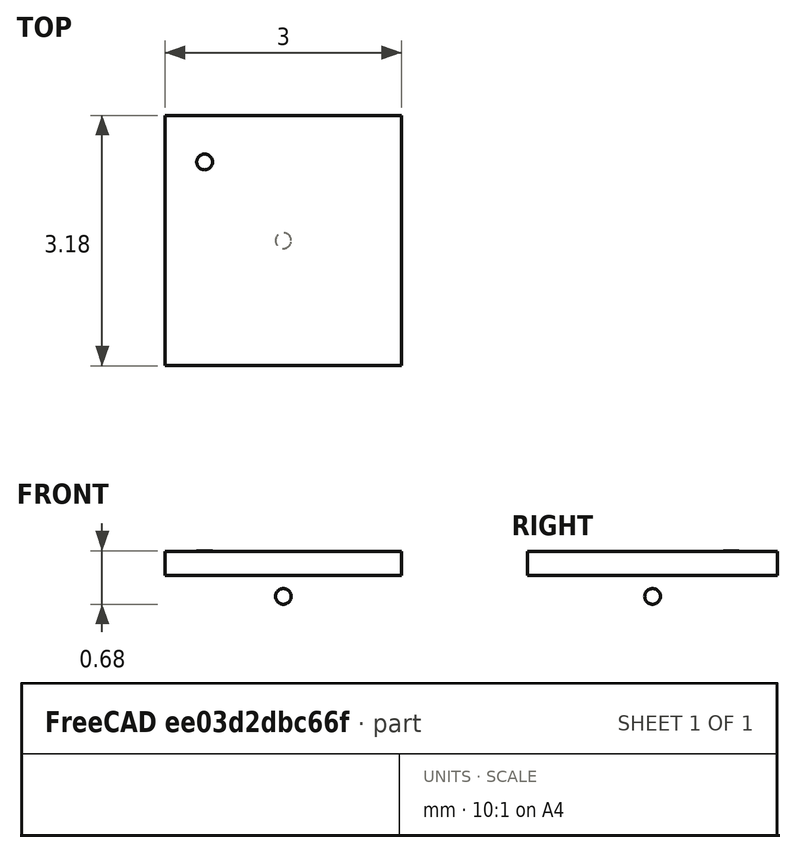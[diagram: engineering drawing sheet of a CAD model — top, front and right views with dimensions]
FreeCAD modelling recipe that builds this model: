
FCSTD DOCUMENT  (FreeCAD 1.0R39109 (Git))
Label: Nordic_WLCSP_3.175x3.175mm_P0.35mm
License: All rights reserved
LicenseURL: https://en.wikipedia.org/wiki/All_rights_reserved
objects: App::LinkElement×81, Sketcher::SketchObject×1, PartDesign::Pad×1, PartDesign::Body×1, Part::Sphere×1, Part::Cylinder×1, Part::FeaturePython×1, App::Part×1
note: 8 computed .brp shape members not serialized (recipe doc carries the construction recipe); baked Part::Feature solids carry a one-line shape summary decoded from their .brp

FEATURE [Sketcher::SketchObject] Sketch
  ArcFitTolerance = 1e-06
  AttachmentSupport = -> [XY_Plane001]
  FullyConstrained = true
  MakeInternals = false
  MapMode = 5
  sketch-geometry (5):
    g0: LineSegment StartX=-1.5 StartY=-1.5875 StartZ=0 EndX=1.5 EndY=-1.5875 EndZ=0
    g1: LineSegment StartX=1.5 StartY=-1.5875 StartZ=0 EndX=1.5 EndY=1.5875 EndZ=0
    g2: LineSegment StartX=1.5 StartY=1.5875 StartZ=0 EndX=-1.5 EndY=1.5875 EndZ=0
    g3: LineSegment StartX=-1.5 StartY=1.5875 StartZ=0 EndX=-1.5 EndY=-1.5875 EndZ=0
    g4: GeomPoint [constr] X=0 Y=0 Z=0
  constraints (12):
    c: Coincident(g0,g1)
    c: Coincident(g1,g2)
    c: Coincident(g2,g3)
    c: Coincident(g3,g0)
    c: Horizontal(g0)
    c: Horizontal(g2)
    c: Vertical(g1)
    c: Vertical(g3)
    c: Symmetric(g2,g0,g4)
    c: Distance(g1,g3) = 3
    c: Distance(g0,g2) = 3.175
    c: Coincident(g4,g-1)
FEATURE [PartDesign::Pad] Pad
  Direction = (0,0,1)
  Length = 0.3
  Length2 = 10
  Profile = -> Sketch
  ReferenceAxis = -> Sketch [N_Axis]
  Refine = true
  Suppressed = false
  Type = 0
FEATURE [PartDesign::Body] Body
  AllowCompound = false
  Group = -> [Sketch,Pad]
  Origin = -> Origin001
  Placement = pos=(0,0,0.18) rot=(0,0,1;0rad)
  Tip = -> Pad
FEATURE [Part::Sphere] Sphere
  Angle1 = -90
  Angle2 = 90
  Angle3 = 360
  AttacherType = Attacher::AttachEngine3D
  Placement = pos=(0,0,-0.089) rot=(0,0,1;0rad)
  Radius = 0.1
FEATURE [Part::Cylinder] Cylinder
  Angle = 360
  AttacherType = Attacher::AttachEngine3D
  FirstAngle = 0
  Height = 0.02
  Placement = pos=(-1,1,0.47) rot=(0,0,1;0rad)
  Radius = 0.1
  SecondAngle = 0
FEATURE [App::LinkElement] Array_i0
  LinkPlacement = pos=(0,0,-0.089) rot=(0,0,1;0rad)
  LinkedObject = -> Sphere
  Placement = pos=(0,0,-0.089) rot=(0,0,1;0rad)
  _LinkOwner = 918
FEATURE [App::LinkElement] Array_i1
  LinkPlacement = pos=(0,0.35,-0.089) rot=(0,0,1;0rad)
  LinkedObject = -> Sphere
  Placement = pos=(0,0.35,-0.089) rot=(0,0,1;0rad)
  _LinkOwner = 918
FEATURE [App::LinkElement] Array_i2
  LinkPlacement = pos=(0,0.7,-0.089) rot=(0,0,1;0rad)
  LinkedObject = -> Sphere
  Placement = pos=(0,0.7,-0.089) rot=(0,0,1;0rad)
  _LinkOwner = 918
FEATURE [App::LinkElement] Array_i3
  LinkPlacement = pos=(0,1.05,-0.089) rot=(0,0,1;0rad)
  LinkedObject = -> Sphere
  Placement = pos=(0,1.05,-0.089) rot=(0,0,1;0rad)
  _LinkOwner = 918
FEATURE [App::LinkElement] Array_i4
  LinkPlacement = pos=(0,1.4,-0.089) rot=(0,0,1;0rad)
  LinkedObject = -> Sphere
  Placement = pos=(0,1.4,-0.089) rot=(0,0,1;0rad)
  _LinkOwner = 918
FEATURE [App::LinkElement] Array_i5
  LinkPlacement = pos=(0,1.75,-0.089) rot=(0,0,1;0rad)
  LinkedObject = -> Sphere
  Placement = pos=(0,1.75,-0.089) rot=(0,0,1;0rad)
  _LinkOwner = 918
FEATURE [App::LinkElement] Array_i6
  LinkPlacement = pos=(0,2.1,-0.089) rot=(0,0,1;0rad)
  LinkedObject = -> Sphere
  Placement = pos=(0,2.1,-0.089) rot=(0,0,1;0rad)
  _LinkOwner = 918
FEATURE [App::LinkElement] Array_i7
  LinkPlacement = pos=(0,2.45,-0.089) rot=(0,0,1;0rad)
  LinkedObject = -> Sphere
  Placement = pos=(0,2.45,-0.089) rot=(0,0,1;0rad)
  _LinkOwner = 918
FEATURE [App::LinkElement] Array_i8
  LinkPlacement = pos=(0,2.8,-0.089) rot=(0,0,1;0rad)
  LinkedObject = -> Sphere
  Placement = pos=(0,2.8,-0.089) rot=(0,0,1;0rad)
  _LinkOwner = 918
FEATURE [App::LinkElement] Array_i9
  LinkPlacement = pos=(0.35,0,-0.089) rot=(0,0,1;0rad)
  LinkedObject = -> Sphere
  Placement = pos=(0.35,0,-0.089) rot=(0,0,1;0rad)
  _LinkOwner = 918
FEATURE [App::LinkElement] Array_i10
  LinkPlacement = pos=(0.35,0.35,-0.089) rot=(0,0,1;0rad)
  LinkedObject = -> Sphere
  Placement = pos=(0.35,0.35,-0.089) rot=(0,0,1;0rad)
  _LinkOwner = 918
FEATURE [App::LinkElement] Array_i11
  LinkPlacement = pos=(0.35,0.7,-0.089) rot=(0,0,1;0rad)
  LinkedObject = -> Sphere
  Placement = pos=(0.35,0.7,-0.089) rot=(0,0,1;0rad)
  _LinkOwner = 918
FEATURE [App::LinkElement] Array_i12
  LinkPlacement = pos=(0.35,1.05,-0.089) rot=(0,0,1;0rad)
  LinkedObject = -> Sphere
  Placement = pos=(0.35,1.05,-0.089) rot=(0,0,1;0rad)
  _LinkOwner = 918
FEATURE [App::LinkElement] Array_i13
  LinkPlacement = pos=(0.35,1.4,-0.089) rot=(0,0,1;0rad)
  LinkedObject = -> Sphere
  Placement = pos=(0.35,1.4,-0.089) rot=(0,0,1;0rad)
  _LinkOwner = 918
FEATURE [App::LinkElement] Array_i14
  LinkPlacement = pos=(0.35,1.75,-0.089) rot=(0,0,1;0rad)
  LinkedObject = -> Sphere
  Placement = pos=(0.35,1.75,-0.089) rot=(0,0,1;0rad)
  _LinkOwner = 918
FEATURE [App::LinkElement] Array_i15
  LinkPlacement = pos=(0.35,2.1,-0.089) rot=(0,0,1;0rad)
  LinkedObject = -> Sphere
  Placement = pos=(0.35,2.1,-0.089) rot=(0,0,1;0rad)
  _LinkOwner = 918
FEATURE [App::LinkElement] Array_i16
  LinkPlacement = pos=(0.35,2.45,-0.089) rot=(0,0,1;0rad)
  LinkedObject = -> Sphere
  Placement = pos=(0.35,2.45,-0.089) rot=(0,0,1;0rad)
  _LinkOwner = 918
FEATURE [App::LinkElement] Array_i17
  LinkPlacement = pos=(0.35,2.8,-0.089) rot=(0,0,1;0rad)
  LinkedObject = -> Sphere
  Placement = pos=(0.35,2.8,-0.089) rot=(0,0,1;0rad)
  _LinkOwner = 918
FEATURE [App::LinkElement] Array_i18
  LinkPlacement = pos=(0.7,0,-0.089) rot=(0,0,1;0rad)
  LinkedObject = -> Sphere
  Placement = pos=(0.7,0,-0.089) rot=(0,0,1;0rad)
  _LinkOwner = 918
FEATURE [App::LinkElement] Array_i19
  LinkPlacement = pos=(0.7,0.35,-0.089) rot=(0,0,1;0rad)
  LinkedObject = -> Sphere
  Placement = pos=(0.7,0.35,-0.089) rot=(0,0,1;0rad)
  _LinkOwner = 918
FEATURE [App::LinkElement] Array_i20
  LinkPlacement = pos=(0.7,0.7,-0.089) rot=(0,0,1;0rad)
  LinkedObject = -> Sphere
  Placement = pos=(0.7,0.7,-0.089) rot=(0,0,1;0rad)
  _LinkOwner = 918
FEATURE [App::LinkElement] Array_i21
  LinkPlacement = pos=(0.7,1.05,-0.089) rot=(0,0,1;0rad)
  LinkedObject = -> Sphere
  Placement = pos=(0.7,1.05,-0.089) rot=(0,0,1;0rad)
  _LinkOwner = 918
FEATURE [App::LinkElement] Array_i22
  LinkPlacement = pos=(0.7,1.4,-0.089) rot=(0,0,1;0rad)
  LinkedObject = -> Sphere
  Placement = pos=(0.7,1.4,-0.089) rot=(0,0,1;0rad)
  _LinkOwner = 918
FEATURE [App::LinkElement] Array_i23
  LinkPlacement = pos=(0.7,1.75,-0.089) rot=(0,0,1;0rad)
  LinkedObject = -> Sphere
  Placement = pos=(0.7,1.75,-0.089) rot=(0,0,1;0rad)
  _LinkOwner = 918
FEATURE [App::LinkElement] Array_i24
  LinkPlacement = pos=(0.7,2.1,-0.089) rot=(0,0,1;0rad)
  LinkedObject = -> Sphere
  Placement = pos=(0.7,2.1,-0.089) rot=(0,0,1;0rad)
  _LinkOwner = 918
FEATURE [App::LinkElement] Array_i25
  LinkPlacement = pos=(0.7,2.45,-0.089) rot=(0,0,1;0rad)
  LinkedObject = -> Sphere
  Placement = pos=(0.7,2.45,-0.089) rot=(0,0,1;0rad)
  _LinkOwner = 918
FEATURE [App::LinkElement] Array_i26
  LinkPlacement = pos=(0.7,2.8,-0.089) rot=(0,0,1;0rad)
  LinkedObject = -> Sphere
  Placement = pos=(0.7,2.8,-0.089) rot=(0,0,1;0rad)
  _LinkOwner = 918
FEATURE [App::LinkElement] Array_i27
  LinkPlacement = pos=(1.05,0,-0.089) rot=(0,0,1;0rad)
  LinkedObject = -> Sphere
  Placement = pos=(1.05,0,-0.089) rot=(0,0,1;0rad)
  _LinkOwner = 918
FEATURE [App::LinkElement] Array_i28
  LinkPlacement = pos=(1.05,0.35,-0.089) rot=(0,0,1;0rad)
  LinkedObject = -> Sphere
  Placement = pos=(1.05,0.35,-0.089) rot=(0,0,1;0rad)
  _LinkOwner = 918
FEATURE [App::LinkElement] Array_i29
  LinkPlacement = pos=(1.05,0.7,-0.089) rot=(0,0,1;0rad)
  LinkedObject = -> Sphere
  Placement = pos=(1.05,0.7,-0.089) rot=(0,0,1;0rad)
  _LinkOwner = 918
FEATURE [App::LinkElement] Array_i30
  LinkPlacement = pos=(1.05,1.05,-0.089) rot=(0,0,1;0rad)
  LinkedObject = -> Sphere
  Placement = pos=(1.05,1.05,-0.089) rot=(0,0,1;0rad)
  _LinkOwner = 918
FEATURE [App::LinkElement] Array_i31
  LinkPlacement = pos=(1.05,1.4,-0.089) rot=(0,0,1;0rad)
  LinkedObject = -> Sphere
  Placement = pos=(1.05,1.4,-0.089) rot=(0,0,1;0rad)
  _LinkOwner = 918
FEATURE [App::LinkElement] Array_i32
  LinkPlacement = pos=(1.05,1.75,-0.089) rot=(0,0,1;0rad)
  LinkedObject = -> Sphere
  Placement = pos=(1.05,1.75,-0.089) rot=(0,0,1;0rad)
  _LinkOwner = 918
FEATURE [App::LinkElement] Array_i33
  LinkPlacement = pos=(1.05,2.1,-0.089) rot=(0,0,1;0rad)
  LinkedObject = -> Sphere
  Placement = pos=(1.05,2.1,-0.089) rot=(0,0,1;0rad)
  _LinkOwner = 918
FEATURE [App::LinkElement] Array_i34
  LinkPlacement = pos=(1.05,2.45,-0.089) rot=(0,0,1;0rad)
  LinkedObject = -> Sphere
  Placement = pos=(1.05,2.45,-0.089) rot=(0,0,1;0rad)
  _LinkOwner = 918
FEATURE [App::LinkElement] Array_i35
  LinkPlacement = pos=(1.05,2.8,-0.089) rot=(0,0,1;0rad)
  LinkedObject = -> Sphere
  Placement = pos=(1.05,2.8,-0.089) rot=(0,0,1;0rad)
  _LinkOwner = 918
FEATURE [App::LinkElement] Array_i36
  LinkPlacement = pos=(1.4,0,-0.089) rot=(0,0,1;0rad)
  LinkedObject = -> Sphere
  Placement = pos=(1.4,0,-0.089) rot=(0,0,1;0rad)
  _LinkOwner = 918
FEATURE [App::LinkElement] Array_i37
  LinkPlacement = pos=(1.4,0.35,-0.089) rot=(0,0,1;0rad)
  LinkedObject = -> Sphere
  Placement = pos=(1.4,0.35,-0.089) rot=(0,0,1;0rad)
  _LinkOwner = 918
FEATURE [App::LinkElement] Array_i38
  LinkPlacement = pos=(1.4,0.7,-0.089) rot=(0,0,1;0rad)
  LinkedObject = -> Sphere
  Placement = pos=(1.4,0.7,-0.089) rot=(0,0,1;0rad)
  _LinkOwner = 918
FEATURE [App::LinkElement] Array_i39
  LinkPlacement = pos=(1.4,1.05,-0.089) rot=(0,0,1;0rad)
  LinkedObject = -> Sphere
  Placement = pos=(1.4,1.05,-0.089) rot=(0,0,1;0rad)
  _LinkOwner = 918
FEATURE [App::LinkElement] Array_i40
  LinkPlacement = pos=(1.4,1.4,-0.089) rot=(0,0,1;0rad)
  LinkedObject = -> Sphere
  Placement = pos=(1.4,1.4,-0.089) rot=(0,0,1;0rad)
  _LinkOwner = 918
FEATURE [App::LinkElement] Array_i41
  LinkPlacement = pos=(1.4,1.75,-0.089) rot=(0,0,1;0rad)
  LinkedObject = -> Sphere
  Placement = pos=(1.4,1.75,-0.089) rot=(0,0,1;0rad)
  _LinkOwner = 918
FEATURE [App::LinkElement] Array_i42
  LinkPlacement = pos=(1.4,2.1,-0.089) rot=(0,0,1;0rad)
  LinkedObject = -> Sphere
  Placement = pos=(1.4,2.1,-0.089) rot=(0,0,1;0rad)
  _LinkOwner = 918
FEATURE [App::LinkElement] Array_i43
  LinkPlacement = pos=(1.4,2.45,-0.089) rot=(0,0,1;0rad)
  LinkedObject = -> Sphere
  Placement = pos=(1.4,2.45,-0.089) rot=(0,0,1;0rad)
  _LinkOwner = 918
FEATURE [App::LinkElement] Array_i44
  LinkPlacement = pos=(1.4,2.8,-0.089) rot=(0,0,1;0rad)
  LinkedObject = -> Sphere
  Placement = pos=(1.4,2.8,-0.089) rot=(0,0,1;0rad)
  _LinkOwner = 918
FEATURE [App::LinkElement] Array_i45
  LinkPlacement = pos=(1.75,0,-0.089) rot=(0,0,1;0rad)
  LinkedObject = -> Sphere
  Placement = pos=(1.75,0,-0.089) rot=(0,0,1;0rad)
  _LinkOwner = 918
FEATURE [App::LinkElement] Array_i46
  LinkPlacement = pos=(1.75,0.35,-0.089) rot=(0,0,1;0rad)
  LinkedObject = -> Sphere
  Placement = pos=(1.75,0.35,-0.089) rot=(0,0,1;0rad)
  _LinkOwner = 918
FEATURE [App::LinkElement] Array_i47
  LinkPlacement = pos=(1.75,0.7,-0.089) rot=(0,0,1;0rad)
  LinkedObject = -> Sphere
  Placement = pos=(1.75,0.7,-0.089) rot=(0,0,1;0rad)
  _LinkOwner = 918
FEATURE [App::LinkElement] Array_i48
  LinkPlacement = pos=(1.75,1.05,-0.089) rot=(0,0,1;0rad)
  LinkedObject = -> Sphere
  Placement = pos=(1.75,1.05,-0.089) rot=(0,0,1;0rad)
  _LinkOwner = 918
FEATURE [App::LinkElement] Array_i49
  LinkPlacement = pos=(1.75,1.4,-0.089) rot=(0,0,1;0rad)
  LinkedObject = -> Sphere
  Placement = pos=(1.75,1.4,-0.089) rot=(0,0,1;0rad)
  _LinkOwner = 918
FEATURE [App::LinkElement] Array_i50
  LinkPlacement = pos=(1.75,1.75,-0.089) rot=(0,0,1;0rad)
  LinkedObject = -> Sphere
  Placement = pos=(1.75,1.75,-0.089) rot=(0,0,1;0rad)
  _LinkOwner = 918
FEATURE [App::LinkElement] Array_i51
  LinkPlacement = pos=(1.75,2.1,-0.089) rot=(0,0,1;0rad)
  LinkedObject = -> Sphere
  Placement = pos=(1.75,2.1,-0.089) rot=(0,0,1;0rad)
  _LinkOwner = 918
FEATURE [App::LinkElement] Array_i52
  LinkPlacement = pos=(1.75,2.45,-0.089) rot=(0,0,1;0rad)
  LinkedObject = -> Sphere
  Placement = pos=(1.75,2.45,-0.089) rot=(0,0,1;0rad)
  _LinkOwner = 918
FEATURE [App::LinkElement] Array_i53
  LinkPlacement = pos=(1.75,2.8,-0.089) rot=(0,0,1;0rad)
  LinkedObject = -> Sphere
  Placement = pos=(1.75,2.8,-0.089) rot=(0,0,1;0rad)
  _LinkOwner = 918
FEATURE [App::LinkElement] Array_i54
  LinkPlacement = pos=(2.1,0,-0.089) rot=(0,0,1;0rad)
  LinkedObject = -> Sphere
  Placement = pos=(2.1,0,-0.089) rot=(0,0,1;0rad)
  _LinkOwner = 918
FEATURE [App::LinkElement] Array_i55
  LinkPlacement = pos=(2.1,0.35,-0.089) rot=(0,0,1;0rad)
  LinkedObject = -> Sphere
  Placement = pos=(2.1,0.35,-0.089) rot=(0,0,1;0rad)
  _LinkOwner = 918
FEATURE [App::LinkElement] Array_i56
  LinkPlacement = pos=(2.1,0.7,-0.089) rot=(0,0,1;0rad)
  LinkedObject = -> Sphere
  Placement = pos=(2.1,0.7,-0.089) rot=(0,0,1;0rad)
  _LinkOwner = 918
FEATURE [App::LinkElement] Array_i57
  LinkPlacement = pos=(2.1,1.05,-0.089) rot=(0,0,1;0rad)
  LinkedObject = -> Sphere
  Placement = pos=(2.1,1.05,-0.089) rot=(0,0,1;0rad)
  _LinkOwner = 918
FEATURE [App::LinkElement] Array_i58
  LinkPlacement = pos=(2.1,1.4,-0.089) rot=(0,0,1;0rad)
  LinkedObject = -> Sphere
  Placement = pos=(2.1,1.4,-0.089) rot=(0,0,1;0rad)
  _LinkOwner = 918
FEATURE [App::LinkElement] Array_i59
  LinkPlacement = pos=(2.1,1.75,-0.089) rot=(0,0,1;0rad)
  LinkedObject = -> Sphere
  Placement = pos=(2.1,1.75,-0.089) rot=(0,0,1;0rad)
  _LinkOwner = 918
FEATURE [App::LinkElement] Array_i60
  LinkPlacement = pos=(2.1,2.1,-0.089) rot=(0,0,1;0rad)
  LinkedObject = -> Sphere
  Placement = pos=(2.1,2.1,-0.089) rot=(0,0,1;0rad)
  _LinkOwner = 918
FEATURE [App::LinkElement] Array_i61
  LinkPlacement = pos=(2.1,2.45,-0.089) rot=(0,0,1;0rad)
  LinkedObject = -> Sphere
  Placement = pos=(2.1,2.45,-0.089) rot=(0,0,1;0rad)
  _LinkOwner = 918
FEATURE [App::LinkElement] Array_i62
  LinkPlacement = pos=(2.1,2.8,-0.089) rot=(0,0,1;0rad)
  LinkedObject = -> Sphere
  Placement = pos=(2.1,2.8,-0.089) rot=(0,0,1;0rad)
  _LinkOwner = 918
FEATURE [App::LinkElement] Array_i63
  LinkPlacement = pos=(2.45,0,-0.089) rot=(0,0,1;0rad)
  LinkedObject = -> Sphere
  Placement = pos=(2.45,0,-0.089) rot=(0,0,1;0rad)
  _LinkOwner = 918
FEATURE [App::LinkElement] Array_i64
  LinkPlacement = pos=(2.45,0.35,-0.089) rot=(0,0,1;0rad)
  LinkedObject = -> Sphere
  Placement = pos=(2.45,0.35,-0.089) rot=(0,0,1;0rad)
  _LinkOwner = 918
FEATURE [App::LinkElement] Array_i65
  LinkPlacement = pos=(2.45,0.7,-0.089) rot=(0,0,1;0rad)
  LinkedObject = -> Sphere
  Placement = pos=(2.45,0.7,-0.089) rot=(0,0,1;0rad)
  _LinkOwner = 918
FEATURE [App::LinkElement] Array_i66
  LinkPlacement = pos=(2.45,1.05,-0.089) rot=(0,0,1;0rad)
  LinkedObject = -> Sphere
  Placement = pos=(2.45,1.05,-0.089) rot=(0,0,1;0rad)
  _LinkOwner = 918
FEATURE [App::LinkElement] Array_i67
  LinkPlacement = pos=(2.45,1.4,-0.089) rot=(0,0,1;0rad)
  LinkedObject = -> Sphere
  Placement = pos=(2.45,1.4,-0.089) rot=(0,0,1;0rad)
  _LinkOwner = 918
FEATURE [App::LinkElement] Array_i68
  LinkPlacement = pos=(2.45,1.75,-0.089) rot=(0,0,1;0rad)
  LinkedObject = -> Sphere
  Placement = pos=(2.45,1.75,-0.089) rot=(0,0,1;0rad)
  _LinkOwner = 918
FEATURE [App::LinkElement] Array_i69
  LinkPlacement = pos=(2.45,2.1,-0.089) rot=(0,0,1;0rad)
  LinkedObject = -> Sphere
  Placement = pos=(2.45,2.1,-0.089) rot=(0,0,1;0rad)
  _LinkOwner = 918
FEATURE [App::LinkElement] Array_i70
  LinkPlacement = pos=(2.45,2.45,-0.089) rot=(0,0,1;0rad)
  LinkedObject = -> Sphere
  Placement = pos=(2.45,2.45,-0.089) rot=(0,0,1;0rad)
  _LinkOwner = 918
FEATURE [App::LinkElement] Array_i71
  LinkPlacement = pos=(2.45,2.8,-0.089) rot=(0,0,1;0rad)
  LinkedObject = -> Sphere
  Placement = pos=(2.45,2.8,-0.089) rot=(0,0,1;0rad)
  _LinkOwner = 918
FEATURE [App::LinkElement] Array_i72
  LinkPlacement = pos=(2.8,0,-0.089) rot=(0,0,1;0rad)
  LinkedObject = -> Sphere
  Placement = pos=(2.8,0,-0.089) rot=(0,0,1;0rad)
  _LinkOwner = 918
FEATURE [App::LinkElement] Array_i73
  LinkPlacement = pos=(2.8,0.35,-0.089) rot=(0,0,1;0rad)
  LinkedObject = -> Sphere
  Placement = pos=(2.8,0.35,-0.089) rot=(0,0,1;0rad)
  _LinkOwner = 918
FEATURE [App::LinkElement] Array_i74
  LinkPlacement = pos=(2.8,0.7,-0.089) rot=(0,0,1;0rad)
  LinkedObject = -> Sphere
  Placement = pos=(2.8,0.7,-0.089) rot=(0,0,1;0rad)
  _LinkOwner = 918
FEATURE [App::LinkElement] Array_i75
  LinkPlacement = pos=(2.8,1.05,-0.089) rot=(0,0,1;0rad)
  LinkedObject = -> Sphere
  Placement = pos=(2.8,1.05,-0.089) rot=(0,0,1;0rad)
  _LinkOwner = 918
FEATURE [App::LinkElement] Array_i76
  LinkPlacement = pos=(2.8,1.4,-0.089) rot=(0,0,1;0rad)
  LinkedObject = -> Sphere
  Placement = pos=(2.8,1.4,-0.089) rot=(0,0,1;0rad)
  _LinkOwner = 918
FEATURE [App::LinkElement] Array_i77
  LinkPlacement = pos=(2.8,1.75,-0.089) rot=(0,0,1;0rad)
  LinkedObject = -> Sphere
  Placement = pos=(2.8,1.75,-0.089) rot=(0,0,1;0rad)
  _LinkOwner = 918
FEATURE [App::LinkElement] Array_i78
  LinkPlacement = pos=(2.8,2.1,-0.089) rot=(0,0,1;0rad)
  LinkedObject = -> Sphere
  Placement = pos=(2.8,2.1,-0.089) rot=(0,0,1;0rad)
  _LinkOwner = 918
FEATURE [App::LinkElement] Array_i79
  LinkPlacement = pos=(2.8,2.45,-0.089) rot=(0,0,1;0rad)
  LinkedObject = -> Sphere
  Placement = pos=(2.8,2.45,-0.089) rot=(0,0,1;0rad)
  _LinkOwner = 918
FEATURE [App::LinkElement] Array_i80
  LinkPlacement = pos=(2.8,2.8,-0.089) rot=(0,0,1;0rad)
  LinkedObject = -> Sphere
  Placement = pos=(2.8,2.8,-0.089) rot=(0,0,1;0rad)
  _LinkOwner = 918
FEATURE [Part::FeaturePython] Array  # Draft array (typed FeaturePython)
  AlwaysSyncPlacement = false
  Angle = 360
  ArrayType = 0
  Axis = (0,0,1)
  Base = -> Sphere
  Center = (0,0,0)
  Count = 81
  ElementList = -> [Array_i0,Array_i1,Array_i2,Array_i3,Array_i4,Array_i5,Array_i6,Array_i7,Array_i8,Array_i9,Array_i10,Array_i11,Array_i12,Array_i13,Array_i14,Array_i15,Array_i16,Array_i17,Array_i18,Array_i19,Array_i20,Array_i21,Array_i22,Array_i23,Array_i24,Array_i25,Array_i26,Array_i27,Array_i28,Array_i29,Array_i30,Array_i31,Array_i32,Array_i33,Array_i34,Array_i35,Array_i36,Array_i37,Array_i38,Array_i39,Array_i40,+40 more]
  ExpandArray = true
  Fuse = false
  IntervalAxis = (0,0,0)
  IntervalX = (0.35,0,0)
  IntervalY = (0,0.35,0)
  IntervalZ = (0,0,100)
  NumberCircles = 3
  NumberPolar = 5
  NumberX = 9
  NumberY = 9
  NumberZ = 1
  Placement = pos=(-1.4,-1.4,0.18) rot=(0,0,1;0rad)
  RadialDistance = 50
  Symmetry = 1
  TangentialDistance = 25
FEATURE [App::Part] Part
  Group = -> [Body,Sphere,Array,Cylinder]
  Origin = -> Origin
